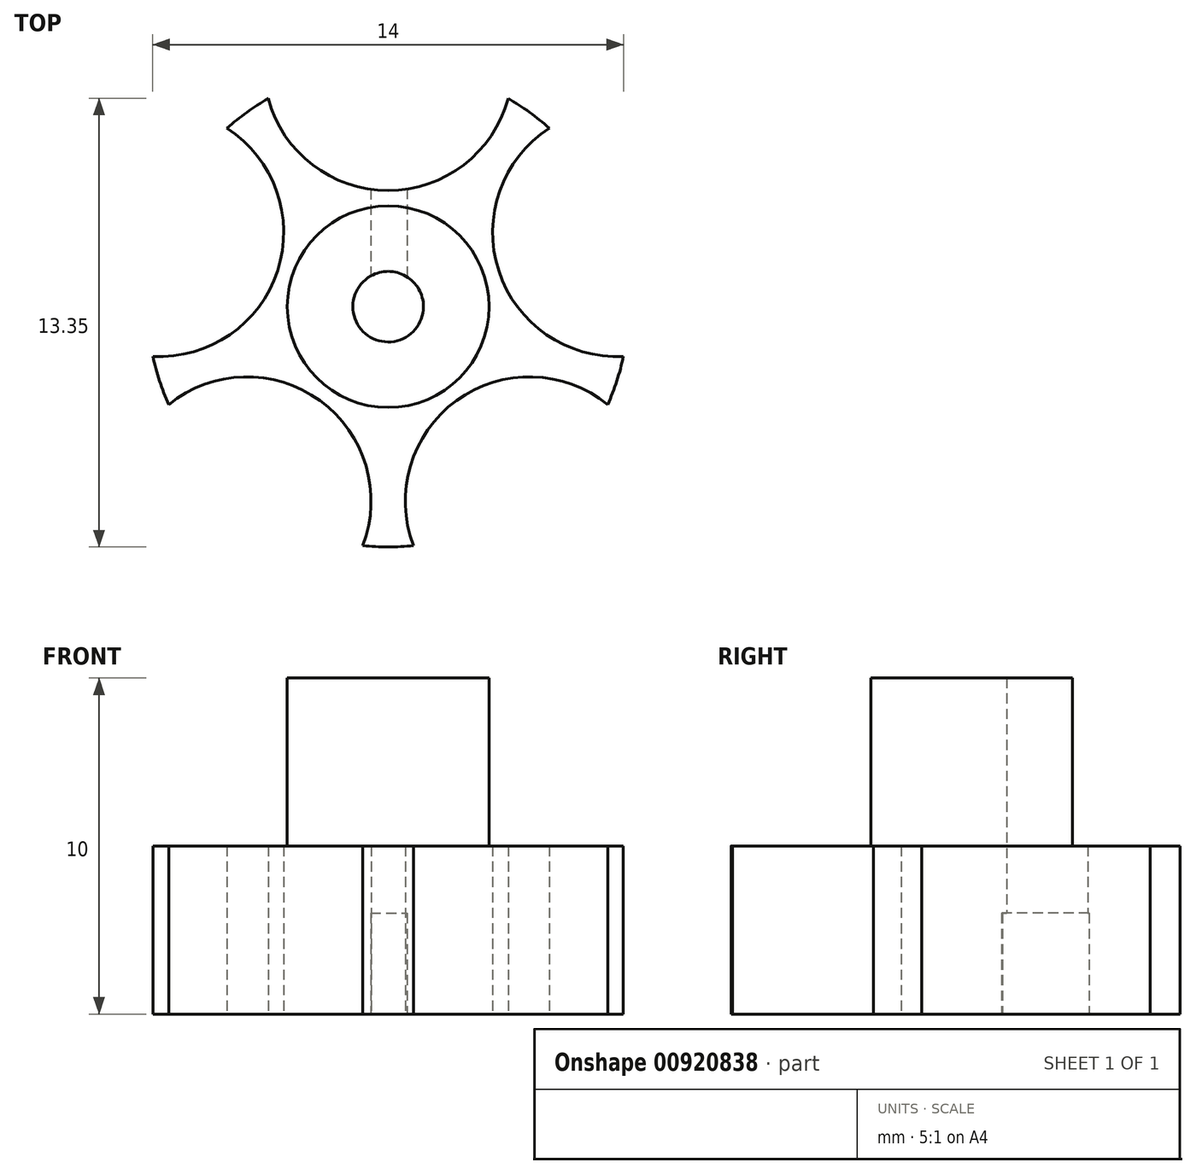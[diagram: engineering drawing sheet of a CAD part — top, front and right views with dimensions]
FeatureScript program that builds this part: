
annotation { "Feature Type Name" : "Feature", "Feature Type Description" : "" }
export const myFeature = defineFeature(function(context is Context, id is Id, definition is map)
    precondition{}
    {
        {
            var Q0;
            Q0=qCreatedBy(makeId("Top.planeOp"),FACE);
            var sketch = newSketch(context, id + "F0", { "sketchPlane" : qUnion([Q0])});
            skCircle(sketch, "E0", {"center": v(0, 0) * mm, "radius": 1.05 * mm});
            skCircle(sketch, "E1", {"center": v(0, 0) * mm, "radius": 7.15 * mm});
            skCircle(sketch, "E2", {"center": v(0, 0) * mm, "radius": 3 * mm});
            skCircle(sketch, "E3", {"center": v(0, 7.15) * mm, "radius": 3.7 * mm});
            skCircle(sketch, "E4.1.0", {"center": v(-6.8, 2.2) * mm, "radius": 3.7 * mm});
            skCircle(sketch, "E4.2.0", {"center": v(-4.2, -5.78) * mm, "radius": 3.7 * mm});
            skCircle(sketch, "E4.3.0", {"center": v(4.2, -5.78) * mm, "radius": 3.7 * mm});
            skCircle(sketch, "E4.4.0", {"center": v(6.8, 2.2) * mm, "radius": 3.7 * mm});
            skLineSegment(sketch, "E5", {"start": v(0, 7.15) * mm, "end": v(0, 0) * mm, "construction": true});
            skLineSegment(sketch, "E6", {"start": v(-0.52, 3.5) * mm, "end": v(-0.52, 0.91) * mm});
            skLineSegment(sketch, "E7", {"start": v(0.56, 3.5) * mm, "end": v(0.56, 0.89) * mm});
            skSolve(sketch);
        }
        {
            var Q0;
            {var subQ1=sQuery(id+"F0.wireOp",EDGE,"E1");var subQ8=sQuery(id+"F0.wireOp",EDGE,"E3");var subQ10=makeQuery(id+"F0.imprint","INTERSECT",VERTEX,{"disambiguationData":[OD(0.0)],"derivedFrom":[subQ1,subQ8]});Q0=makeQuery(id+"F0.imprint","IMPRINT",FACE,{"disambiguationData":[TD([[makeQuery(id+"F0.imprint","IMPRINT",EDGE,{"disambiguationData":[TD([[subQ10,1.0]])],"derivedFrom":subQ1}),1.0]])]});}
            var Q1;
            {var subQ0=sQuery(id+"F0.wireOp",EDGE,"E6");var subQ1=sQuery(id+"F0.wireOp",EDGE,"E2");var subQ2=makeQuery(id+"F0.imprint","INTERSECT",VERTEX,{"derivedFrom":[subQ1,subQ0]});Q1=makeQuery(id+"F0.imprint","IMPRINT",FACE,{"disambiguationData":[TD([[makeQuery(id+"F0.imprint","IMPRINT",EDGE,{"disambiguationData":[TD([[subQ2,1.0]])],"derivedFrom":subQ1}),-1.0]])]});}
            extrude(context, id + "F1", {"entities" : qUnion([Q0, Q1]), "depth" : 5 * mm, "offsetDistance" : 25 * mm});
        }
        {
            var Q0;
            {var subQ0=sQuery(id+"F0.wireOp",EDGE,"E6");var subQ1=sQuery(id+"F0.wireOp",EDGE,"E0");var subQ2=makeQuery(id+"F0.imprint","INTERSECT",VERTEX,{"derivedFrom":[subQ1,subQ0]});Q0=makeQuery(id+"F0.imprint","IMPRINT",FACE,{"disambiguationData":[TD([[makeQuery(id+"F0.imprint","IMPRINT",EDGE,{"disambiguationData":[TD([[subQ2,-1.0]])],"derivedFrom":subQ1}),-1.0]])]});}
            var Q1;
            {var subQ0=sQuery(id+"F0.wireOp",EDGE,"E6");var subQ1=sQuery(id+"F0.wireOp",EDGE,"E0");var subQ2=makeQuery(id+"F0.imprint","INTERSECT",VERTEX,{"derivedFrom":[subQ1,subQ0]});Q1=makeQuery(id+"F0.imprint","IMPRINT",FACE,{"disambiguationData":[TD([[makeQuery(id+"F0.imprint","IMPRINT",EDGE,{"disambiguationData":[TD([[subQ2,1.0]])],"derivedFrom":subQ1}),-1.0]])]});}
            extrude(context, id + "F2", {"entities" : qUnion([Q0, Q1]), "operationType" : NewBodyOperationType.ADD, "depth" : 10 * mm, "offsetDistance" : 25 * mm});
        }
        {
            var Q0;
            {var subQ0=sQuery(id+"F0.wireOp",EDGE,"E6");var subQ1=sQuery(id+"F0.wireOp",EDGE,"E0");var subQ2=makeQuery(id+"F0.imprint","INTERSECT",VERTEX,{"derivedFrom":[subQ1,subQ0]});Q0=makeQuery(id+"F0.imprint","IMPRINT",FACE,{"disambiguationData":[TD([[makeQuery(id+"F0.imprint","IMPRINT",EDGE,{"disambiguationData":[TD([[subQ2,1.0]])],"derivedFrom":subQ1}),-1.0]])]});}
            var Q1;
            {var subQ0=sQuery(id+"F0.wireOp",EDGE,"E6");var subQ1=sQuery(id+"F0.wireOp",EDGE,"E2");var subQ2=makeQuery(id+"F0.imprint","INTERSECT",VERTEX,{"derivedFrom":[subQ1,subQ0]});Q1=makeQuery(id+"F0.imprint","IMPRINT",FACE,{"disambiguationData":[TD([[makeQuery(id+"F0.imprint","IMPRINT",EDGE,{"disambiguationData":[TD([[subQ2,1.0]])],"derivedFrom":subQ1}),-1.0]])]});}
            extrude(context, id + "F3", {"entities" : qUnion([Q0, Q1]), "operationType" : NewBodyOperationType.REMOVE, "depth" : 3 * mm, "offsetDistance" : 25 * mm});
        }
    });
